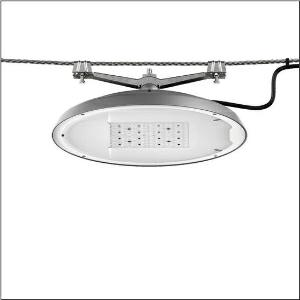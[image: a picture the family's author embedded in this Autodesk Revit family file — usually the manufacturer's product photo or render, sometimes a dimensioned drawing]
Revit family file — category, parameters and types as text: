
# Revit family: dl_r__50_iq_mini___st0_8s_5xa248v31f08me_3f47
name_source: partatom
category: Lighting Fixtures
units: mm (PartAtom-declared; Revit-internal decimal feet)

## family parameters
Cut with Voids When Loaded = No
Host = Face
Light Source = No
Part Type = Normal
Room Calculation Point = No
Round Connector Dimension = Use Diameter
Shared = No

## types (1)
- --- (1 x LED, 15660 lm, 107.8 W, 3000K)
    Apparent Load = 108 VA
    CIE Flux Codes = 38 75 97 100 100
    Color Rendering = 70
    Color Temperature = 3000K
    Default Elevation = 1800 mm
    Description = DL® 50 iQ mini, catenary luminaire, primary light control with lens, of PMMA, primary optical cover: cover, of toughened safety glass, transparent, light distribution: ST0.8s, light emission: direct distribution, primary light characteristic: symmetric, installation type: suspended mounting, LED, High Power LED, rated luminous flux: 15.660lm, luminous efficacy: 145lm/W, light colour: 730, colour temperature: 3000K, control: optimised constant luminous flux control (CLO 2.0), Desk-Remote (wireless, voltage-free reading and setting of iQ features in the workshop via application-optimized NFC function/RFID function), Light-Fading, Smart-Wire, Night-Set, Lumen-Switch, Temp-Guard, Auto-Match, Street-Remote, mains connection: 230..240V, AC, 50/60Hz, start of lifetime: 108W, end of service life: 118W, reduction: 47W, luminaire housing, of diecast aluminium, powder-coated, Siteco® metallic grey (DB 702S), diameter: 500mm, height: 115mm, protection rating (complete): IP66, insulation class (complete): insulation class II (safety insulation), certification: CE, ENEC, ENEC+, VDE, impact resistance: IK08, permissible operating ambient temperature for outdoor applications: -25..+40°C, standard-compliant lighting for roads and squares, packaging unit: 1 piece

Light Distribution: ST0.8s
    Height = 124 mm  [stored 0.406824 ft]
    Lamp = 1 x LED
    Lamp Light Flux = 15660 lm
    Lamp Power = 107.8 W
    Lamp count = 1
    Length = 500 mm
    Luminous efficacy = 145 lm/W
    Manufacturer = Siteco
    ModVariant = No
    Model = 5XA248V31F08ME
    Number of Poles = 1
    OnlyDefault = Yes
    Power Factor = 1
    Product Name = DL® 50 iQ mini | ST0.8s
    Product group = catenary luminaire
    ProductGroupID = 6300
    Protection Class = Protection class II
    Protection Degree = IP 66
    RLX_Detail_Level = 1
    RLX_Emergency_Light_Flux = 0 lm
    RLX_Emergency_Type = 0
    RLX_Emergency_Type_DB = No
    RlxData = <blob elided: 127189 chars, md5=928970ef>
    Socket = socket
    Standby Power = 0 W
    System Light Flux = 15660 lm
    System Power = 108 W
    Type Comments = factory setting: luminous flux: 100 % | dim-lin: 254 | 565 mA
    Type Image = l_1251783.jpg
    URL = http://relux.com
    VarID = @adj_110785
    Voltage = 0 V
    Weight = 0.00 kg
    Width = 0 mm  [stored 0 ft]

note: [stored X ft] marks values corroborated as IEEE doubles in the binary element streams (Revit-internal decimal feet)

## geometry (parser evidence)
native form markers: Blend x4, Sweep x13
no freeform markers — native parametric forms only
